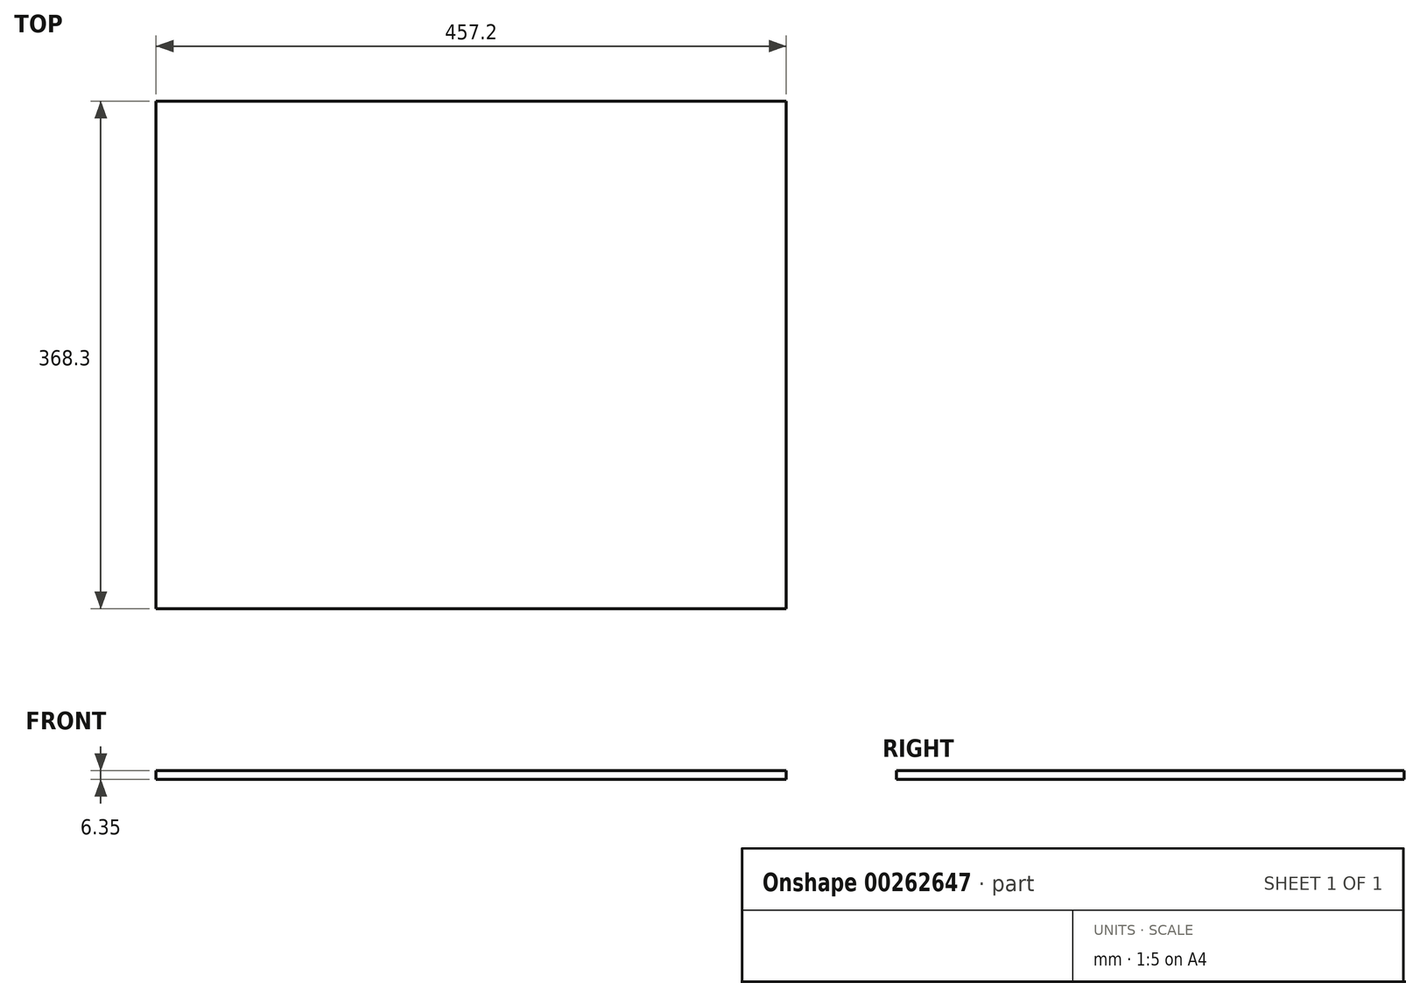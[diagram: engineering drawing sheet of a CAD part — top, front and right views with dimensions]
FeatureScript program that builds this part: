
annotation { "Feature Type Name" : "Feature", "Feature Type Description" : "" }
export const myFeature = defineFeature(function(context is Context, id is Id, definition is map)
    precondition{}
    {
        {
            var Q0;
            Q0=qCreatedBy(makeId("Top.planeOp"),FACE);
            var sketch = newSketch(context, id + "F0", { "sketchPlane" : qUnion([Q0])});
            skLineSegment(sketch, "E0.bottom", {"start": v(0, 0) * mm, "end": v(457.2, 0) * mm});
            skLineSegment(sketch, "E0.top", {"start": v(0, 368.3) * mm, "end": v(457.2, 368.3) * mm});
            skLineSegment(sketch, "E0.left", {"start": v(0, 0) * mm, "end": v(0, 368.3) * mm});
            skLineSegment(sketch, "E0.right", {"start": v(457.2, 0) * mm, "end": v(457.2, 368.3) * mm});
            skSolve(sketch);
        }
        {
            var Q0;
            Q0=makeQuery(id+"F0.imprint","IMPRINT",FACE,{"disambiguationData":[TD([[makeQuery(id+"F0.imprint","IMPRINT",EDGE,{"derivedFrom":sQuery(id+"F0.wireOp",EDGE,"E0.bottom")}),1.0]])]});
            extrude(context, id + "F1", {"entities" : qUnion([Q0]), "depth" : 6.35 * mm});
        }
    });
